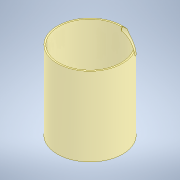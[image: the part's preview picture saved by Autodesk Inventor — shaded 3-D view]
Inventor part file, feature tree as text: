
AUTODESK INVENTOR PART (.ipt)
format: ipt  version: 2022 (Build 260153000, 153)  size: 195,072 bytes
history: native  units: mm
features: extrude x10, sketch x7, plane x3
ambient origin geometry x8: Origin, YZ Plane, XZ Plane, XY Plane, X Axis, Y Axis, Z Axis, Center Point
bodies: Solid1 (feature_tree)
feature tree (20):
  sketch  "Sketch1"  dims[d0=73.0mm d1=70.0mm]
  extrude  "Extrusion1"  Depth=70.0mm
  extrude  "Extrusion2"  Depth=120.0mm TaperAngle=0.0deg
  extrude  "Extrusion3"  Depth=46.2mm
  extrude  "Extrusion4"  Depth=2.0mm
  extrude  "Extrusion5"  Depth=19.5mm
  extrude  "Extrusion6"  Depth=18.0mm
  plane  "Work Plane2"
  sketch  "Sketch8"  dims[d14=2.0mm d15=0.0mm d16=19.5mm]
  extrude  "Extrusion9"  Depth=10.0mm
  extrude  "Extrusion10"  Depth=36.5mm
  plane  "Work Plane3"
  plane  "Work Plane5"
  extrude  "Extrusion14"  Depth=3.0mm
  extrude  "Extrusion15"  Depth=3.0mm TaperAngle=0.0deg
  sketch  "Sketch3"  dims[d2=3.0mm d3=0.0mm d4=120.0mm d5=0.0mm]
  sketch  "Sketch4"  dims[d9=2.0mm d10=0.0mm d11=46.2mm]
  sketch  "Sketch5"  dims[d12=46.2mm d13=2.0mm]
  sketch  "Sketch13"  dims[d17=7.5mm d18=18.0mm]
  sketch  "Sketch14"  dims[d19=0.0mm d20=0.0mm d21=10.0mm d22=36.5mm d23=16.0mm d24=6.0mm d25=0.0mm d37=36.5mm d38=13.1mm d39=8.5mm d40=0.0mm d41=15.0mm d42=10.5mm d43=15.0mm d44=3.0mm d45=0.0mm d46=1.0mm d47=0.0mm d48=-27.0mm d59=-88.0mm d61=40.0mm d62=3.0mm d63=0.0mm d64=0.0mm d65=0.0mm]
